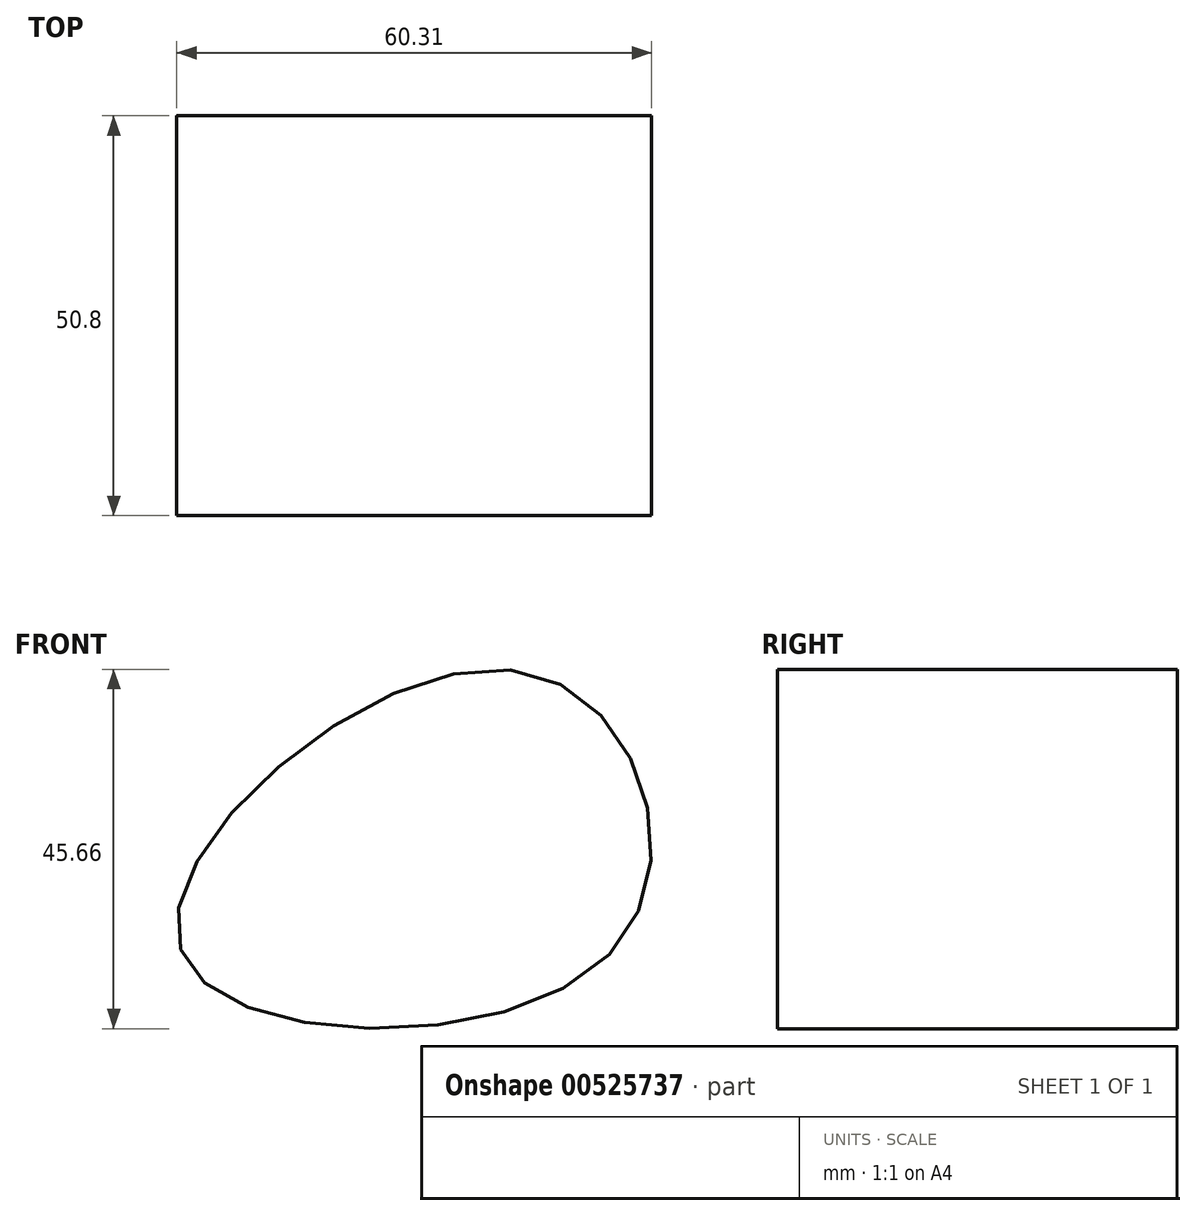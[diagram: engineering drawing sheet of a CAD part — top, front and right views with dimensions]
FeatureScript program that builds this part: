
annotation { "Feature Type Name" : "Feature", "Feature Type Description" : "" }
export const myFeature = defineFeature(function(context is Context, id is Id, definition is map)
    precondition{}
    {
        {
            var Q0;
            Q0=qCreatedBy(makeId("Front.planeOp"),FACE);
            var sketch = newSketch(context, id + "F0", { "sketchPlane" : qUnion([Q0])});
            skFitSpline(sketch, "E0", {"points": [v(0, 0) * mm, v(55.1, 0) * mm, v(43.14, 35.33) * mm, v(0, 0) * mm]});
            skSolve(sketch);
        }
        {
            var Q0;
            Q0 = qSketchRegion(id + "F0", true);
            extrude(context, id + "F1", {"entities" : qUnion([Q0]), "depth" : 50.8 * mm, "offsetDistance" : 25.4 * mm});
        }
    });
